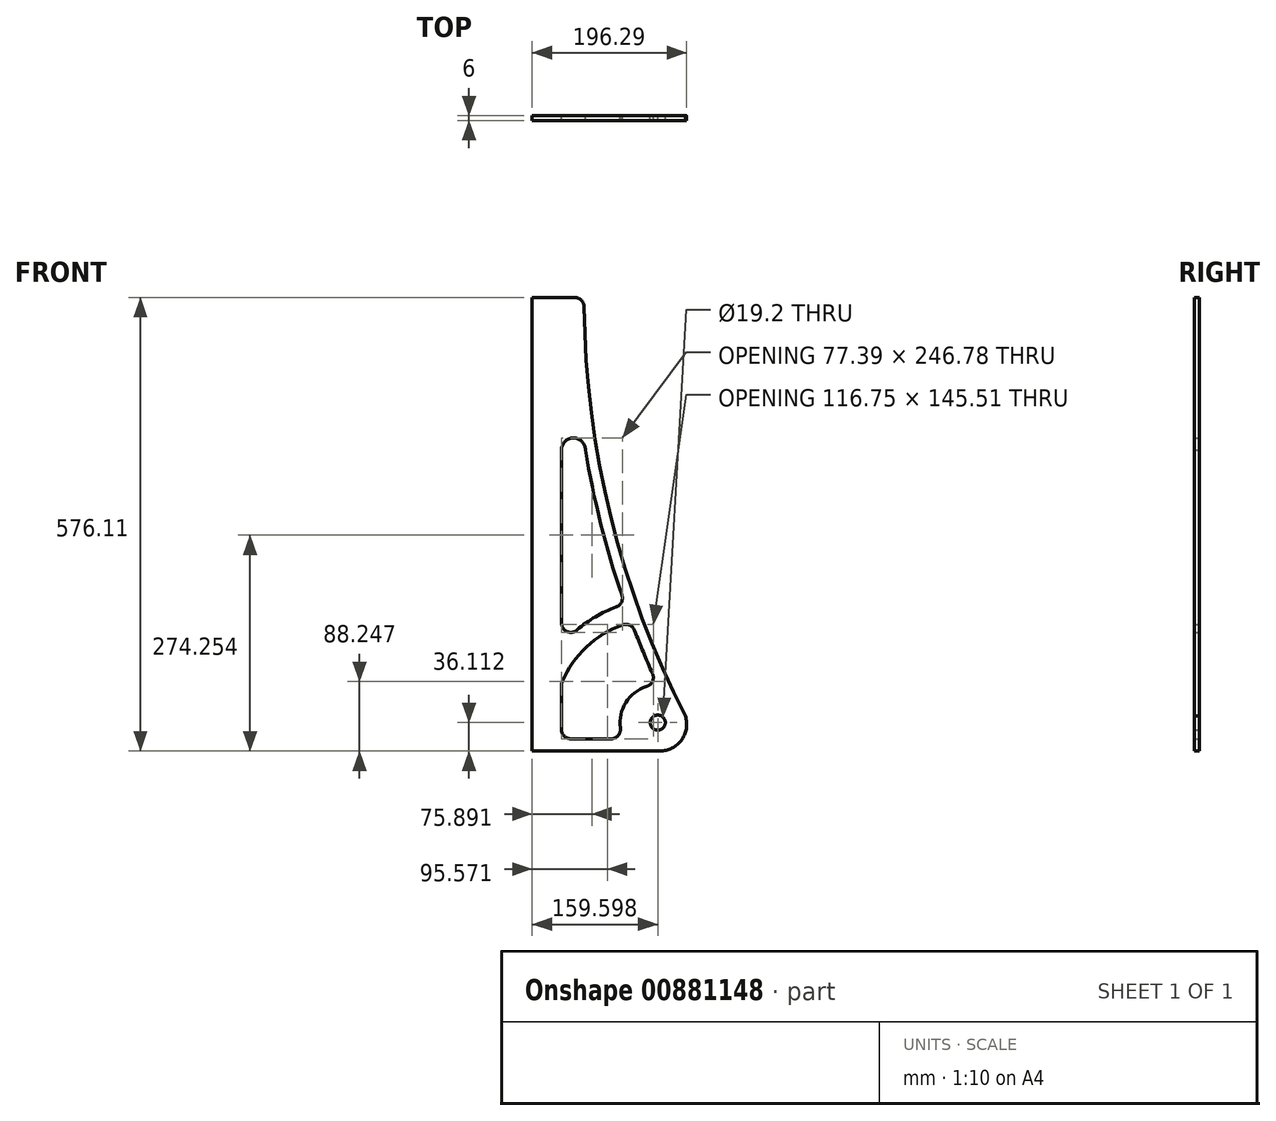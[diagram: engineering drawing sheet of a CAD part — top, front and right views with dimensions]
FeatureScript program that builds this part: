
annotation { "Feature Type Name" : "Feature", "Feature Type Description" : "" }
export const myFeature = defineFeature(function(context is Context, id is Id, definition is map)
    precondition{}
    {
        {
            var Q0;
            Q0=qCreatedBy(makeId("Front.planeOp"),FACE);
            var sketch = newSketch(context, id + "F0", { "sketchPlane" : qUnion([Q0])});
            skLineSegment(sketch, "E0", {"start": v(-47.37, -274.05) * mm, "end": v(-47.37, 301.95) * mm});
            skLineSegment(sketch, "E1", {"start": v(-47.37, 301.95) * mm, "end": v(6.69, 301.95) * mm});
            skArc(sketch, "E2", {"start": v(18.69, 290.07) * mm, "mid": v(15.13, 298.48) * mm, "end": v(6.69, 301.95) * mm});
            skArc(sketch, "E3", {"start": v(18.69, 290.07) * mm, "mid": v(52.64, 22.75) * mm, "end": v(147.22, -229.58) * mm});
            skArc(sketch, "E4", {"start": v(20.27, 108.26) * mm, "mid": v(5.05, 123.49) * mm, "end": v(-10.17, 108.26) * mm});
            skLineSegment(sketch, "E5", {"start": v(-10.17, -111.42) * mm, "end": v(-10.17, 108.26) * mm});
            skArc(sketch, "E6", {"start": v(19.47, 113.14) * mm, "mid": v(39.1, 17.52) * mm, "end": v(66.6, -76.16) * mm});
            skArc(sketch, "E7", {"start": v(66.6, -76.16) * mm, "mid": v(66.05, -85.22) * mm, "end": v(59.3, -91.3) * mm});
            skArc(sketch, "E8", {"start": v(59.3, -91.3) * mm, "mid": v(33.15, -103.57) * mm, "end": v(9.71, -120.46) * mm});
            skArc(sketch, "E9", {"start": v(-10.17, -111.42) * mm, "mid": v(-3.14, -122.34) * mm, "end": v(9.71, -120.46) * mm});
            skArc(sketch, "E10", {"start": v(67.5, -113.86) * mm, "mid": v(21.59, -142.09) * mm, "end": v(-9.21, -186.31) * mm});
            skArc(sketch, "E11", {"start": v(67.5, -113.86) * mm, "mid": v(76.56, -114.23) * mm, "end": v(82.77, -120.84) * mm});
            skArc(sketch, "E12", {"start": v(82.77, -120.84) * mm, "mid": v(93.8, -148.48) * mm, "end": v(105.54, -175.83) * mm});
            skArc(sketch, "E13", {"start": v(105.54, -175.83) * mm, "mid": v(105.5, -185.67) * mm, "end": v(98.1, -192.17) * mm});
            skArc(sketch, "E14", {"start": v(98.1, -192.17) * mm, "mid": v(71.66, -212.39) * mm, "end": v(64.73, -244.94) * mm});
            skArc(sketch, "E15", {"start": v(52.85, -258.67) * mm, "mid": v(61.92, -254.52) * mm, "end": v(64.73, -244.94) * mm});
            skLineSegment(sketch, "E16", {"start": v(52.85, -258.67) * mm, "end": v(1.83, -258.67) * mm});
            skLineSegment(sketch, "E17", {"start": v(-10.17, -246.67) * mm, "end": v(-10.17, -191.02) * mm});
            skArc(sketch, "E18", {"start": v(-10.17, -246.67) * mm, "mid": v(-6.66, -255.15) * mm, "end": v(1.83, -258.67) * mm});
            skLineSegment(sketch, "E19", {"start": v(112.23, -274.05) * mm, "end": v(-47.37, -274.05) * mm});
            skArc(sketch, "E20", {"start": v(112.23, -274.05) * mm, "mid": v(141.66, -261.2) * mm, "end": v(147.22, -229.58) * mm});
            skArc(sketch, "E21", {"start": v(-9.21, -186.31) * mm, "mid": v(-9.93, -188.62) * mm, "end": v(-10.17, -191.02) * mm});
            skCircle(sketch, "E22", {"center": v(112.23, -238.05) * mm, "radius": 9.6 * mm});
            skSolve(sketch);
        }
        {
            var Q0;
            Q0=makeQuery(id+"F0.imprint","IMPRINT",FACE,{"disambiguationData":[TD([[makeQuery(id+"F0.imprint","IMPRINT",EDGE,{"derivedFrom":sQuery(id+"F0.wireOp",EDGE,"E0")}),-1.0]])]});
            extrude(context, id + "F1", {"entities" : qUnion([Q0]), "depth" : 6 * mm, "offsetDistance" : 25 * mm});
        }
    });
